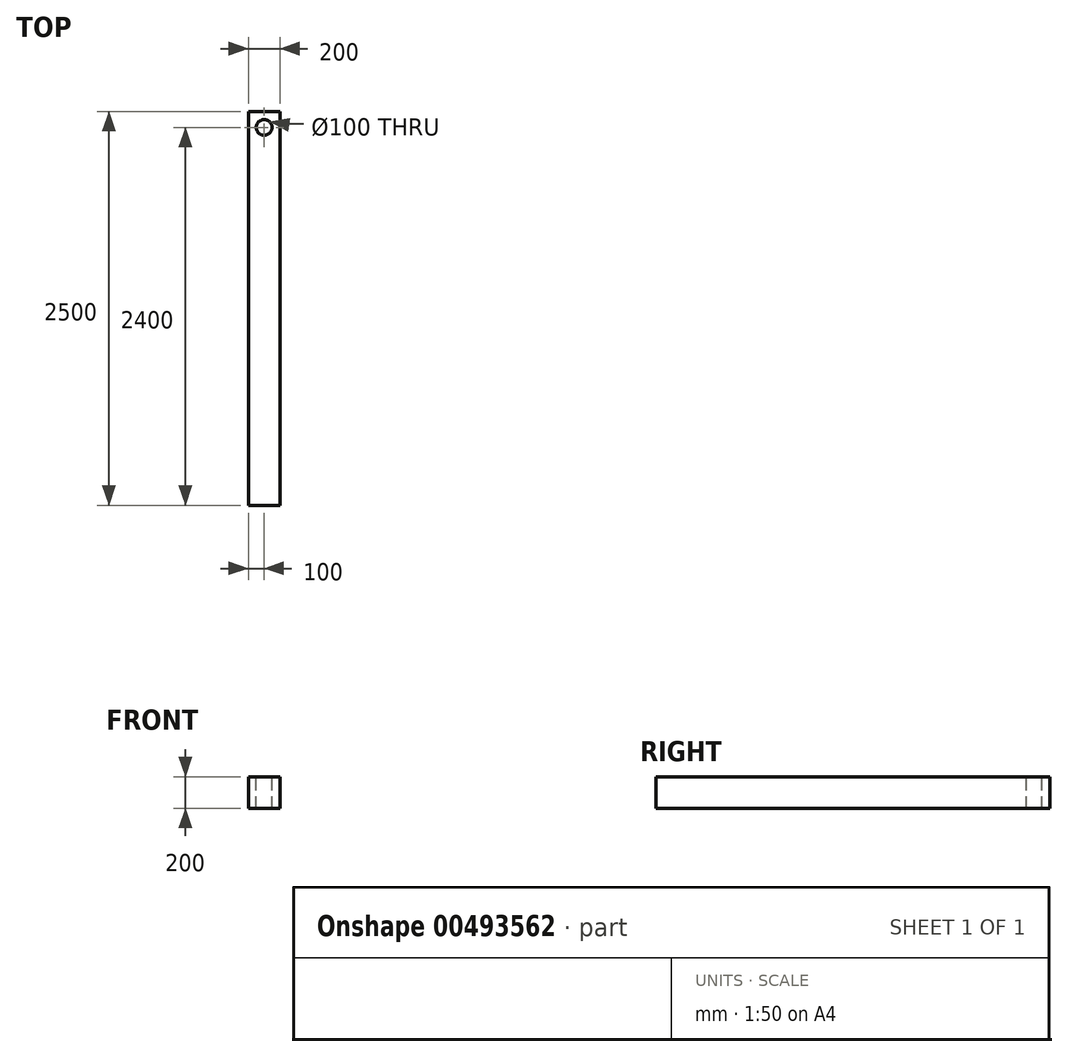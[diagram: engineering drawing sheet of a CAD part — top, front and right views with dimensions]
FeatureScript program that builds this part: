
annotation { "Feature Type Name" : "Feature", "Feature Type Description" : "" }
export const myFeature = defineFeature(function(context is Context, id is Id, definition is map)
    precondition{}
    {
        {
            var Q0;
            Q0=qCreatedBy(makeId("Front.planeOp"),FACE);
            var sketch = newSketch(context, id + "F0", { "sketchPlane" : qUnion([Q0])});
            skLineSegment(sketch, "E0.bottom", {"start": v(-100, 100) * mm, "end": v(100, 100) * mm});
            skLineSegment(sketch, "E0.top", {"start": v(-100, -100) * mm, "end": v(100, -100) * mm});
            skLineSegment(sketch, "E0.left", {"start": v(-100, 100) * mm, "end": v(-100, -100) * mm});
            skLineSegment(sketch, "E0.right", {"start": v(100, 100) * mm, "end": v(100, -100) * mm});
            skSolve(sketch);
        }
        {
            var Q0;
            Q0 = qSketchRegion(id + "F0", true);
            extrude(context, id + "F1", {"entities" : qUnion([Q0]), "endBound" : BoundingType.SYMMETRIC, "depth" : 2500 * mm});
        }
        {
            var Q0;
            Q0=makeQuery(id+"F1.opExtrude","SWEPT_FACE",FACE,{"disambiguationData":[OSD([sQuery(id+"F0.wireOp",EDGE,"E0.bottom")])]});
            var sketch = newSketch(context, id + "F2", { "sketchPlane" : qUnion([Q0])});
            skPoint(sketch, "E1", {"position": v(0, 1150) * mm});
            skSolve(sketch);
        }
        {
            var Q0;
            Q0=sQuery(id+"F2.wireOp",VERTEX,"E1");
            var Q1;
            Q1=makeQuery(id+"F1.opExtrude","SWEPT_BODY",BODY,{"disambiguationData":[OSD([sQuery(id+"F0.wireOp",EDGE,"E0.bottom"),sQuery(id+"F0.wireOp",EDGE,"E0.top"),sQuery(id+"F0.wireOp",EDGE,"E0.left"),sQuery(id+"F0.wireOp",EDGE,"E0.right")])]});
            hole(context, id + "F3", {"style" : HoleStyle.SIMPLE, "endStyle" : HoleEndStyle.BLIND, "holeDiameter" : 100 * mm, "holeDepth" : 200 * mm, "isTappedThrough" : true, "tappedDepth" : 12 * mm, "tapClearance" : 3, "locations" : qUnion([Q0]), "scope" : qUnion([Q1])});
        }
    });
